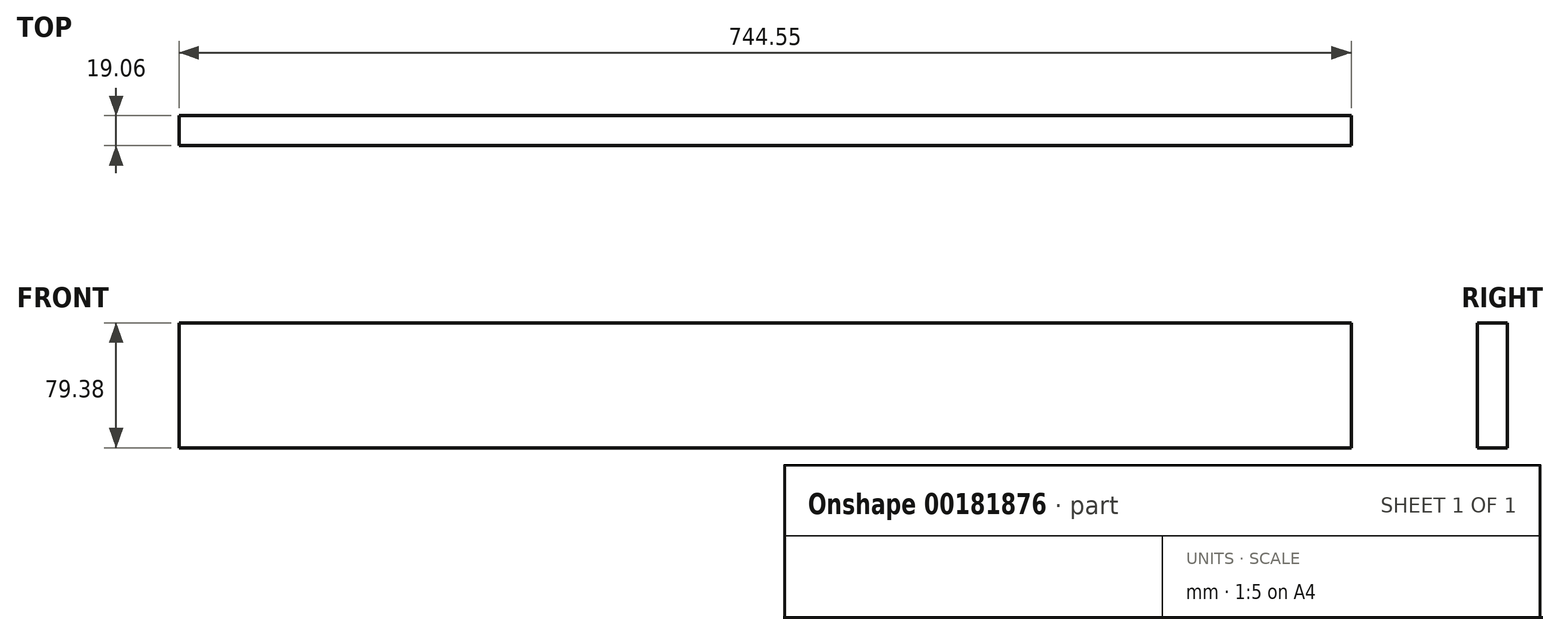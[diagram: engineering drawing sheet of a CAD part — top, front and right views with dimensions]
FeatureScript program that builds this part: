
annotation { "Feature Type Name" : "Feature", "Feature Type Description" : "" }
export const myFeature = defineFeature(function(context is Context, id is Id, definition is map)
    precondition{}
    {
        {
            var Q0;
            Q0=qCreatedBy(makeId("Right.planeOp"),FACE);
            var sketch = newSketch(context, id + "F0", { "sketchPlane" : qUnion([Q0])});
            skLineSegment(sketch, "E0.bottom", {"start": v(9.52, -39.69) * mm, "end": v(-9.53, -39.69) * mm});
            skLineSegment(sketch, "E0.top", {"start": v(9.53, 39.69) * mm, "end": v(-9.52, 39.69) * mm});
            skLineSegment(sketch, "E0.left", {"start": v(9.52, -39.69) * mm, "end": v(9.53, 39.69) * mm});
            skLineSegment(sketch, "E0.right", {"start": v(-9.53, -39.69) * mm, "end": v(-9.52, 39.69) * mm});
            skPoint(sketch, "E0.middle", {"position": v(0, 0) * mm});
            skSolve(sketch);
        }
        {
            var Q0;
            Q0=makeQuery(id+"F0.imprint","IMPRINT",FACE,{"disambiguationData":[TD([[makeQuery(id+"F0.imprint","IMPRINT",EDGE,{"derivedFrom":sQuery(id+"F0.wireOp",EDGE,"E0.bottom")}),-1.0]])]});
            extrude(context, id + "F1", {"entities" : qUnion([Q0]), "depth" : 744.55 * mm});
        }
    });
